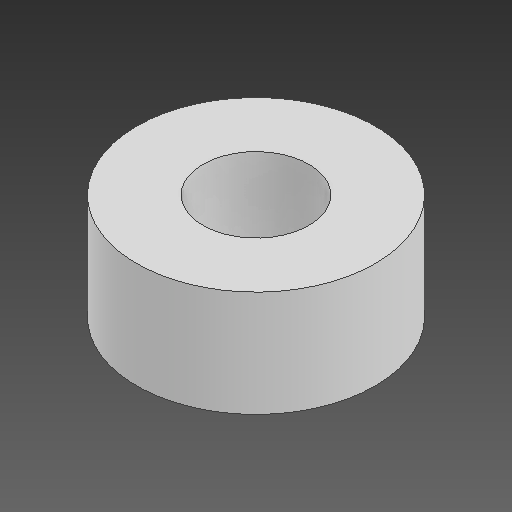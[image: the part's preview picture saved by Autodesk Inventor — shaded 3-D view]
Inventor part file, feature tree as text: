
AUTODESK INVENTOR PART (.ipt)
format: ipt  version: 2021 (Build 250183000, 183)  size: 95,744 bytes
history: native  units: mm
features: extrude x1, sketch x1
ambient origin geometry x8: Origin, YZ Plane, XZ Plane, XY Plane, X Axis, Y Axis, Z Axis, Center Point
bodies: Solid1 (feature_tree)
feature tree (2):
  extrude  "Extrusion1"  Depth=4.0mm
  sketch  "Sketch1"  dims[d0=9.0mm d1=4.0mm d2=4.0mm d3=0.0mm]
